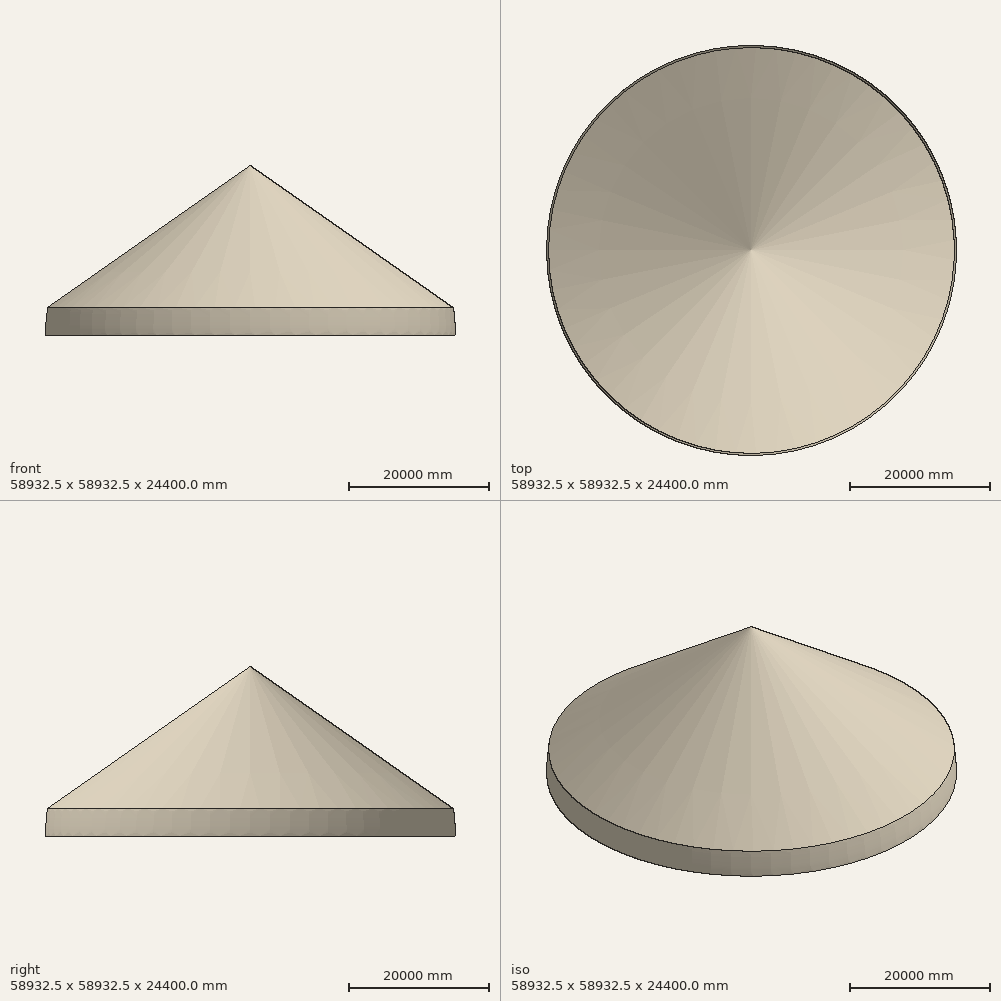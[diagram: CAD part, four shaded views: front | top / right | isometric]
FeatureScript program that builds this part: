
annotation { "Feature Type Name" : "Feature", "Feature Type Description" : "" }
export const myFeature = defineFeature(function(context is Context, id is Id, definition is map)
    precondition{}
    {
        {
            var Q0;
            Q0=qCreatedBy(makeId("Front.planeOp"),FACE);
            var sketch = newSketch(context, id + "F0", { "sketchPlane" : qUnion([Q0])});
            skLineSegment(sketch, "E0", {"start": v(-15015.16, 13056.66) * mm, "end": v(-15015.16, 13448.36) * mm});
            skFitSpline(sketch, "E1", {"points": [v(-9972.71, 12670.2) * mm, v(-11129.3, 12848.78) * mm, v(-12297.8, 12965.88) * mm, v(-13984.56, 13044.64) * mm, v(-14499.86, 13056.66) * mm, v(-15015.16, 13056.66) * mm]});
            skEllipticalArc(sketch, "E2", {});
            skLineSegment(sketch, "E3", {"start": v(-9876.96, 12875.54) * mm, "end": v(-9972.71, 12670.2) * mm});
            skFitSpline(sketch, "E4", {"points": [v(7544.37, 4055.3) * mm, v(7450.4, 4152.33) * mm, v(7355.66, 4248.74) * mm, v(6399, 5208.18) * mm, v(5475.01, 6021.75) * mm, v(3516.84, 7534.97) * mm, v(2482.66, 8234.61) * mm, v(321.55, 9508.09) * mm, v(-805.38, 10081.92) * mm, v(-3132.97, 11094.02) * mm, v(-4333.63, 11532.3) * mm, v(-6788.41, 12265.82) * mm, v(-8042.52, 12561.07) * mm, v(-9500.48, 12815) * mm, v(-9688.56, 12846.08) * mm, v(-9876.96, 12875.54) * mm]});
            skFitSpline(sketch, "E5", {"points": [v(14449.38, -13448.36) * mm, v(14449.38, -12750) * mm, v(14418.26, -12051.62) * mm, v(14253.65, -10207.22) * mm, v(14066.71, -9064.96) * mm, v(13609.24, -7155.05) * mm, v(13381.54, -6379.33) * mm, v(13114.74, -5614.37) * mm]});
            skFitSpline(sketch, "E6", {"points": [v(13114.74, -5614.37) * mm, v(12616.96, -4384.25) * mm, v(11897.97, -2607.48) * mm, v(10638.28, -162.58) * mm, v(9298.64, 1851.33) * mm, v(8162.53, 3278.68) * mm, v(7544.37, 4055.3) * mm]});
            skFitSpline(sketch, "E7", {"points": [v(15015.16, -13448.36) * mm, v(14319.75, -7693.6) * mm, v(12074.37, -1840.16) * mm, v(8706.73, 3044.59) * mm, v(4871.24, 6705.83) * mm, v(0, 9844.89) * mm, v(-6976.14, 12466.72) * mm, v(-12151.5, 13325.8) * mm, v(-15015.15, 13448.36) * mm], "startDerivative": vector(-3136.37, 44782.99) * mm, "endDerivative": vector(-29761.56, 613.59) * mm});
            skLineSegment(sketch, "E8", {"start": v(20036.84, -13448.36) * mm, "end": v(-15015.16, -13448.36) * mm});
            skLineSegment(sketch, "E9", {"start": v(-15015.16, -13448.36) * mm, "end": v(-15015.16, -9485.96) * mm});
            skLineSegment(sketch, "E10", {"start": v(-15015.16, -13448.36) * mm, "end": v(-15015.16, 10951.61) * mm});
            skLineSegment(sketch, "E11", {"start": v(-15015.16, 10951.61) * mm, "end": v(-9299.75, 10951.61) * mm});
            skLineSegment(sketch, "E12", {"start": v(-15015.16, 10951.61) * mm, "end": v(14378.3, -9629.9) * mm});
            skLineSegment(sketch, "E13", {"start": v(-15015.16, -9485.96) * mm, "end": v(14113.73, -9485.96) * mm});
            skLineSegment(sketch, "E14", {"start": v(14449.38, -13448.36) * mm, "end": v(15015.16, -13448.36) * mm});
            const initialGuessF0  = {"E2": [-15.015164167780899, -13.448364428534196, 1, 0, 30.030328335561798, 26.896728857068393, 0, 1.570796]};
            skSetInitialGuess(sketch, initialGuessF0);
            skSolve(sketch);
        }
        {
            var Q0;
            {var subQ0=sQuery(id+"F0.wireOp",EDGE,"E13");Q0=makeQuery(id+"F0.imprint","IMPRINT",FACE,{"disambiguationData":[TD([[makeQuery(id+"F0.imprint","IMPRINT",EDGE,{"derivedFrom":subQ0}),1.0]])]});}
            var Q1;
            {var subQ0=sQuery(id+"F0.wireOp",EDGE,"E8");Q1=makeQuery(id+"F0.imprint","IMPRINT",FACE,{"disambiguationData":[TD([[makeQuery(id+"F0.imprint","IMPRINT",EDGE,{"derivedFrom":subQ0}),-1.0]])]});}
            var Q2;
            Q2=sQuery(id+"F0.wireOp",EDGE,"E10");
            revolve(context, id + "F1", {"entities" : qUnion([Q0, Q1]), "axis" : qUnion([Q2]), "revolveType" : RevolveType.FULL});
        }
    });
